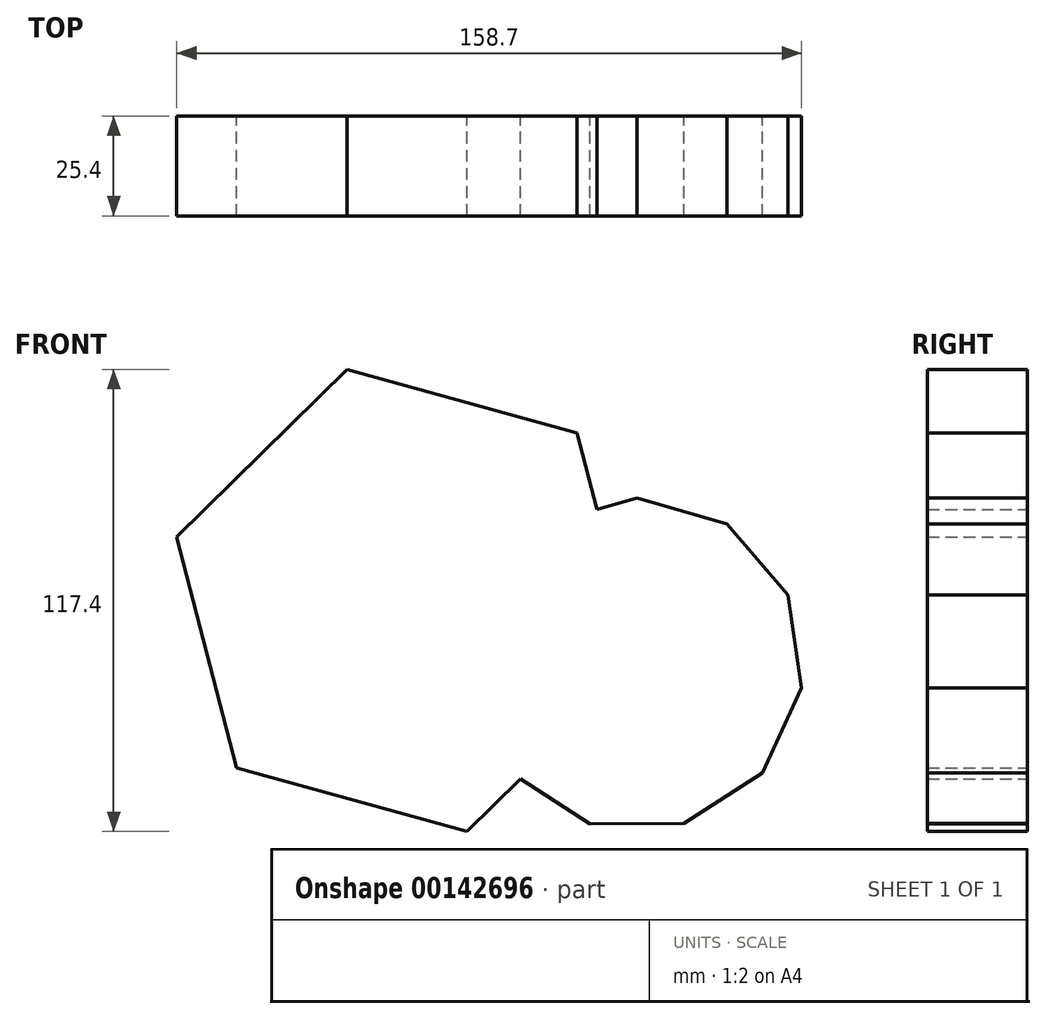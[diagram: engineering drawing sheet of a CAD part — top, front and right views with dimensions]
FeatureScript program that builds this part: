
annotation { "Feature Type Name" : "Feature", "Feature Type Description" : "" }
export const myFeature = defineFeature(function(context is Context, id is Id, definition is map)
    precondition{}
    {
        {
            var Q0;
            Q0=qCreatedBy(makeId("Front.planeOp"),FACE);
            var sketch = newSketch(context, id + "F0", { "sketchPlane" : qUnion([Q0])});
            skCircle(sketch, "E0.cCircle", {"center": v(-36.84, 17.5) * mm, "radius": 52.52 * mm, "construction": true});
            skLineSegment(sketch, "E0.0", {"start": v(21.61, 1.33) * mm, "end": v(-21.61, -41.2) * mm});
            skLineSegment(sketch, "E0.1", {"start": v(-21.61, -41.2) * mm, "end": v(-80.06, -25.04) * mm});
            skLineSegment(sketch, "E0.2", {"start": v(-80.06, -25.04) * mm, "end": v(-95.28, 33.65) * mm});
            skLineSegment(sketch, "E0.3", {"start": v(-95.28, 33.65) * mm, "end": v(-52.06, 76.19) * mm});
            skLineSegment(sketch, "E0.4", {"start": v(-52.06, 76.19) * mm, "end": v(6.39, 60.03) * mm});
            skLineSegment(sketch, "E0.5", {"start": v(6.39, 60.03) * mm, "end": v(21.61, 1.33) * mm});
            skPoint(sketch, "E0.0.midPoint", {"position": v(0, -19.94) * mm});
            skCircle(sketch, "E1.cCircle", {"center": v(21.61, 1.33) * mm, "radius": 40.53 * mm, "construction": true});
            skLineSegment(sketch, "E1.0", {"start": v(60.03, 18.9) * mm, "end": v(63.42, -4.66) * mm});
            skLineSegment(sketch, "E1.1", {"start": v(63.42, -4.66) * mm, "end": v(53.55, -26.32) * mm});
            skLineSegment(sketch, "E1.2", {"start": v(53.55, -26.32) * mm, "end": v(33.53, -39.2) * mm});
            skLineSegment(sketch, "E1.3", {"start": v(33.53, -39.2) * mm, "end": v(9.73, -39.2) * mm});
            skLineSegment(sketch, "E1.4", {"start": v(9.73, -39.2) * mm, "end": v(-10.3, -26.35) * mm});
            skLineSegment(sketch, "E1.5", {"start": v(-10.3, -26.35) * mm, "end": v(-20.2, -4.7) * mm});
            skLineSegment(sketch, "E1.6", {"start": v(-20.2, -4.7) * mm, "end": v(-16.82, 18.86) * mm});
            skLineSegment(sketch, "E1.7", {"start": v(-16.82, 18.86) * mm, "end": v(-1.24, 36.85) * mm});
            skLineSegment(sketch, "E1.8", {"start": v(-1.24, 36.85) * mm, "end": v(21.59, 43.57) * mm});
            skLineSegment(sketch, "E1.9", {"start": v(21.59, 43.57) * mm, "end": v(44.43, 36.87) * mm});
            skLineSegment(sketch, "E1.10", {"start": v(44.43, 36.87) * mm, "end": v(60.03, 18.9) * mm});
            skPoint(sketch, "E1.0.midPoint", {"position": v(61.72, 7.12) * mm});
            skSolve(sketch);
        }
        {
            var Q0;
            Q0 = qSketchRegion(id + "F0", true);
            extrude(context, id + "F1", {"entities" : qUnion([Q0]), "depth" : 25.4 * mm});
        }
    });
